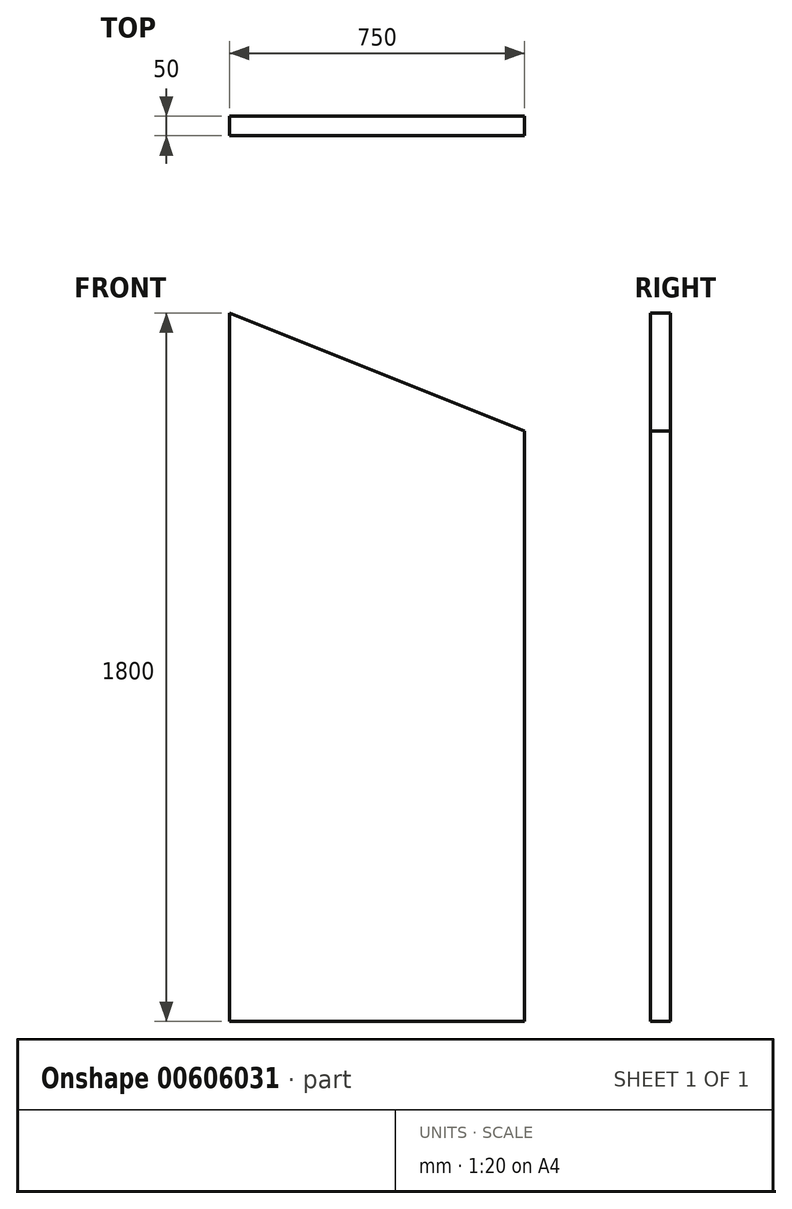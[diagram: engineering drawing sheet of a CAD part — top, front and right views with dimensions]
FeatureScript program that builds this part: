
annotation { "Feature Type Name" : "Feature", "Feature Type Description" : "" }
export const myFeature = defineFeature(function(context is Context, id is Id, definition is map)
    precondition{}
    {
        {
            var Q0;
            Q0=qCreatedBy(makeId("Front.planeOp"),FACE);
            var sketch = newSketch(context, id + "F0", { "sketchPlane" : qUnion([Q0])});
            skLineSegment(sketch, "E0.top", {"start": v(375, -900) * mm, "end": v(-375, -900) * mm});
            skLineSegment(sketch, "E0.right", {"start": v(-375, 900) * mm, "end": v(-375, -900) * mm});
            skPoint(sketch, "E0.middle", {"position": v(0, 0) * mm});
            skLineSegment(sketch, "E1", {"start": v(-375, 900) * mm, "end": v(375, 600) * mm});
            skLineSegment(sketch, "E2", {"start": v(375, 600) * mm, "end": v(375, -900) * mm});
            skSolve(sketch);
        }
        {
            var Q0;
            Q0 = qSketchRegion(id + "F0", true);
            extrude(context, id + "F1", {"entities" : qUnion([Q0]), "depth" : 50 * mm, "offsetDistance" : 25.4 * mm});
        }
    });
